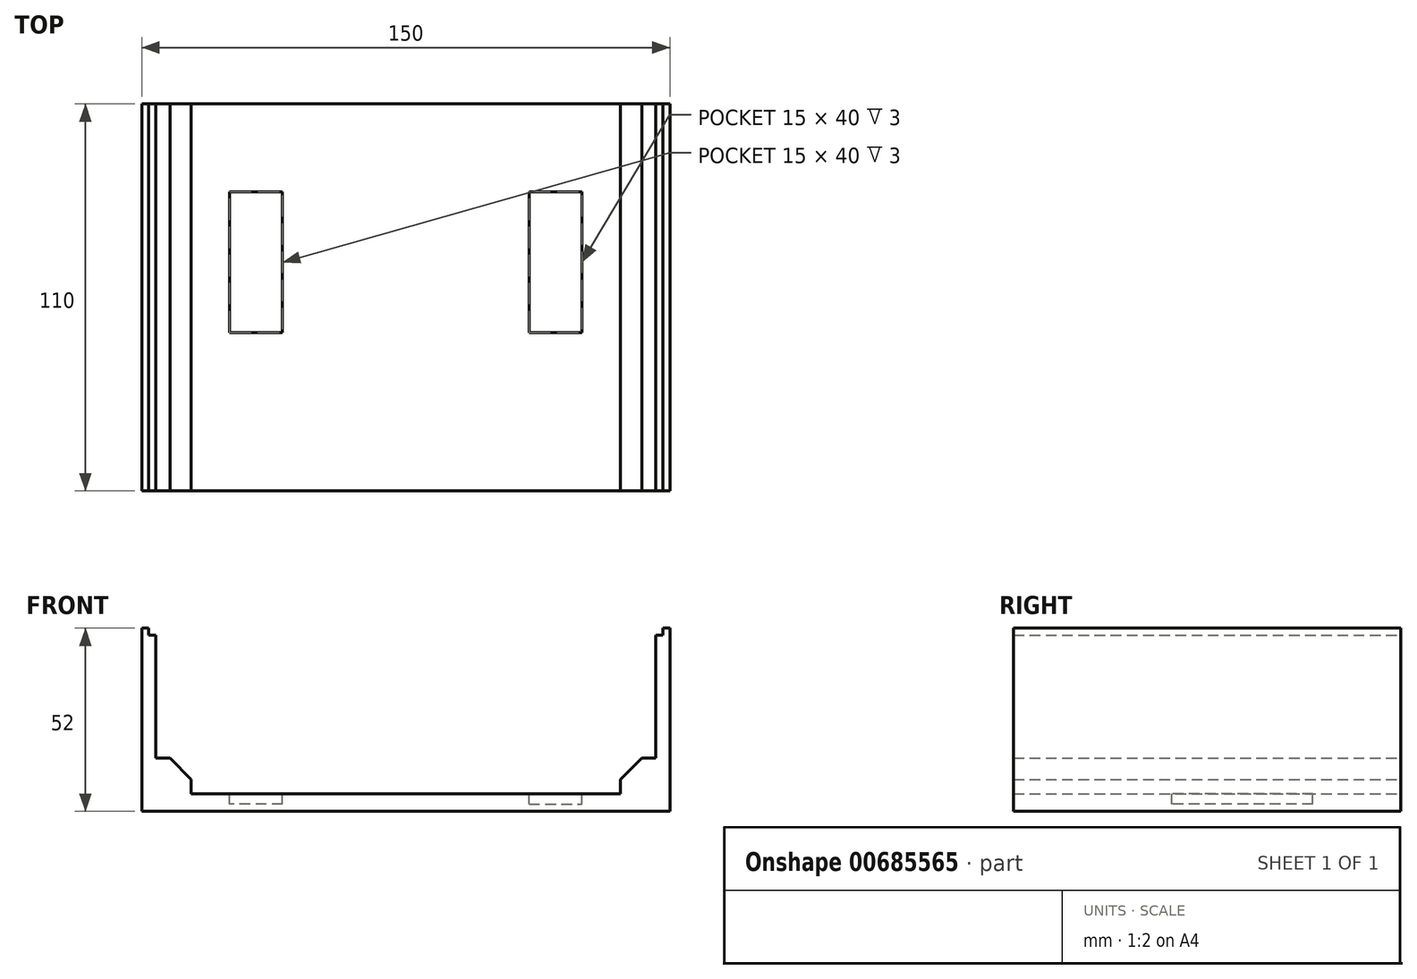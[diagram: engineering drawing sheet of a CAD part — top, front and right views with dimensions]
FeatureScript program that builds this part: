
annotation { "Feature Type Name" : "Feature", "Feature Type Description" : "" }
export const myFeature = defineFeature(function(context is Context, id is Id, definition is map)
    precondition{}
    {
        {
            var Q0;
            Q0=qCreatedBy(makeId("Front.planeOp"),FACE);
            var sketch = newSketch(context, id + "F0", { "sketchPlane" : qUnion([Q0])});
            skLineSegment(sketch, "E0", {"start": v(0, 0) * mm, "end": v(75, 0) * mm});
            skLineSegment(sketch, "E1", {"start": v(75, 0) * mm, "end": v(75, 52) * mm});
            skLineSegment(sketch, "E2", {"start": v(75, 52) * mm, "end": v(73, 52) * mm});
            skLineSegment(sketch, "E3", {"start": v(73, 52) * mm, "end": v(73, 50) * mm});
            skLineSegment(sketch, "E4", {"start": v(73, 50) * mm, "end": v(71, 50) * mm});
            skLineSegment(sketch, "E5", {"start": v(71, 50) * mm, "end": v(71, 8) * mm});
            skLineSegment(sketch, "E6", {"start": v(67, 5) * mm, "end": v(0, 5) * mm});
            skLineSegment(sketch, "E7.MirrorCS", {"start": v(0, 5) * mm, "end": v(0, 0) * mm});
            skLineSegment(sketch, "E8", {"start": v(60.96, 5) * mm, "end": v(60.96, 9) * mm});
            skLineSegment(sketch, "E9", {"start": v(67, 15.04) * mm, "end": v(60.96, 9) * mm});
            skLineSegment(sketch, "E10", {"start": v(67, 15.04) * mm, "end": v(71, 15.04) * mm});
            skSolve(sketch);
        }
        {
            var Q0;
            Q0 = qSketchRegion(id + "F2", true);
            var Q1;
            Q1 = qSketchRegion(id + "F0", true);
            extrude(context, id + "F1", {"entities" : qUnion([Q0, Q1]), "depth" : 110 * mm, "offsetDistance" : 25 * mm});
        }
        {
            var Q0;
            Q0=makeQuery(id+"F1.opExtrude","SWEPT_FACE",FACE,{"disambiguationData":[OSD([sQuery(id+"F0.wireOp",EDGE,"E6")])]});
            var sketch = newSketch(context, id + "F2", { "sketchPlane" : qUnion([Q0])});
            skLineSegment(sketch, "E11", {"start": v(-120.05, -45) * mm, "end": v(146.37, -45) * mm, "construction": true});
            skLineSegment(sketch, "E12.bottom", {"start": v(35, -25) * mm, "end": v(50, -25) * mm});
            skLineSegment(sketch, "E12.top", {"start": v(35, -65) * mm, "end": v(50, -65) * mm});
            skLineSegment(sketch, "E12.left", {"start": v(35, -25) * mm, "end": v(35, -65) * mm});
            skLineSegment(sketch, "E12.right", {"start": v(50, -25) * mm, "end": v(50, -65) * mm});
            skSolve(sketch);
        }
        {
            var Q0;
            Q0=makeQuery(id+"F2.imprint","IMPRINT",FACE,{"disambiguationData":[TD([[makeQuery(id+"F2.imprint","IMPRINT",EDGE,{"derivedFrom":sQuery(id+"F2.wireOp",EDGE,"E12.bottom")}),-1.0]])]});
            extrude(context, id + "F3", {"entities" : qUnion([Q0]), "operationType" : NewBodyOperationType.REMOVE, "oppositeDirection" : true, "depth" : 3 * mm, "offsetDistance" : 25 * mm});
        }
        {
            var Q0;
            Q0=makeQuery(id+"F1.opExtrude","SWEPT_BODY",BODY,{"disambiguationData":[OSD([sQuery(id+"F0.wireOp",EDGE,"E0"),sQuery(id+"F0.wireOp",EDGE,"E1"),sQuery(id+"F0.wireOp",EDGE,"E2"),sQuery(id+"F0.wireOp",EDGE,"E3"),sQuery(id+"F0.wireOp",EDGE,"E4"),sQuery(id+"F0.wireOp",EDGE,"E5"),sQuery(id+"F0.wireOp",EDGE,"J7q4WPWS-mDzM-QFAH-Tumv-eUMRrKuCSJzQ"),sQuery(id+"F0.wireOp",EDGE,"E6"),sQuery(id+"F0.wireOp",EDGE,"E7.MirrorCS")])]});
            var Q1;
            Q1=qCreatedBy(makeId("Right.planeOp"),FACE);
            mirror(context, id + "F4", {"operationType" : NewBodyOperationType.ADD, "entities" : qUnion([Q0]), "mirrorPlane" : qUnion([Q1])});
        }
    });
